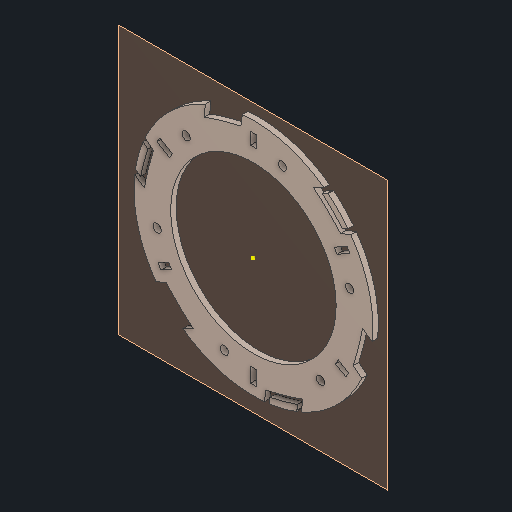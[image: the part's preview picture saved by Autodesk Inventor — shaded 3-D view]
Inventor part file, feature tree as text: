
AUTODESK INVENTOR PART (.ipt)
format: ipt  version: 2023 (Build 270158000, 158)  size: 398,336 bytes
history: native  units: mm
features: reference x17, other x11, sketch x5, extrude x4, pattern_circular x2, plane x1, projected_geometry x1
ambient origin geometry x8: Origin, YZ Plane, XZ Plane, XY Plane, X Axis, Y Axis, Z Axis, Center Point
bodies: Solid1 (feature_tree)
feature tree (41):
  plane  "Work Plane1"
  extrude  "Extrusion1"  Depth=3.0mm TaperAngle=0.0deg
  sketch  "Sketch2"  dims[d3=1.5mm d4=3.0mm d5=0.0mm d6=30.0mm d7=360.0deg]
  extrude  "Extrusion2"  Depth=3.0mm TaperAngle=0.0deg
  pattern_circular  "Circular Pattern1"  Count=3 Angle=360.0deg
  extrude  "Extrusion3"  Depth=10.0mm
  extrude  "Extrusion4"  Depth=10.0mm TaperAngle=360.0deg
  pattern_circular  "Circular Pattern2"  [2 undecoded]
  sketch  "Sketch1"  dims[d0=90.0mm d1=3.0mm d2=0.0mm]
  reference  "Reference1"
  reference  "Reference2"
  reference  "Reference3"
  reference  "Reference4"
  reference  "Reference5"
  reference  "Reference6"
  reference  "Reference7"
  reference  "Reference8"
  reference  "Reference9"
  reference  "Reference10"
  reference  "Reference11"
  reference  "Reference12"
  reference  "Reference13"
  sketch  "Sketch3"  dims[d9=10.0mm d10=0.0mm d11=4.5mm]
  reference  "Reference14"
  sketch  "Sketch4"  dims[d12=10.0mm d13=0.0mm d14=60.0mm d15=360.0deg]
  reference  "Reference15"
  reference  "Reference16"
  projected_geometry  "Projected Loop1"
  reference  "Reference17"
  sketch  "Sketch5"
  parser-record x1  (decoder bookkeeping rows leaked as tree rows — omitted from the tree; the rows remain in map.json)
  other  "assembly.iam"
  other  "vase:1"
  other  "SpantB:3"
  other  "SpantB:2"
  other  "SpantB:1"
  other  "SpantA:2"
  other  "SpantA:3"
  other  "SpantA:1"
  other  "Assembly1"
  other  "vase_v2._tom:1"
note: 2 required parameter values undecoded (feature->parameter linkage not recoverable at this tier; creation-order binding heuristic only, values carry confidence <= 0.55)
note: 1 file-system path scrubbed to <path> (originals preserved in map.json)
